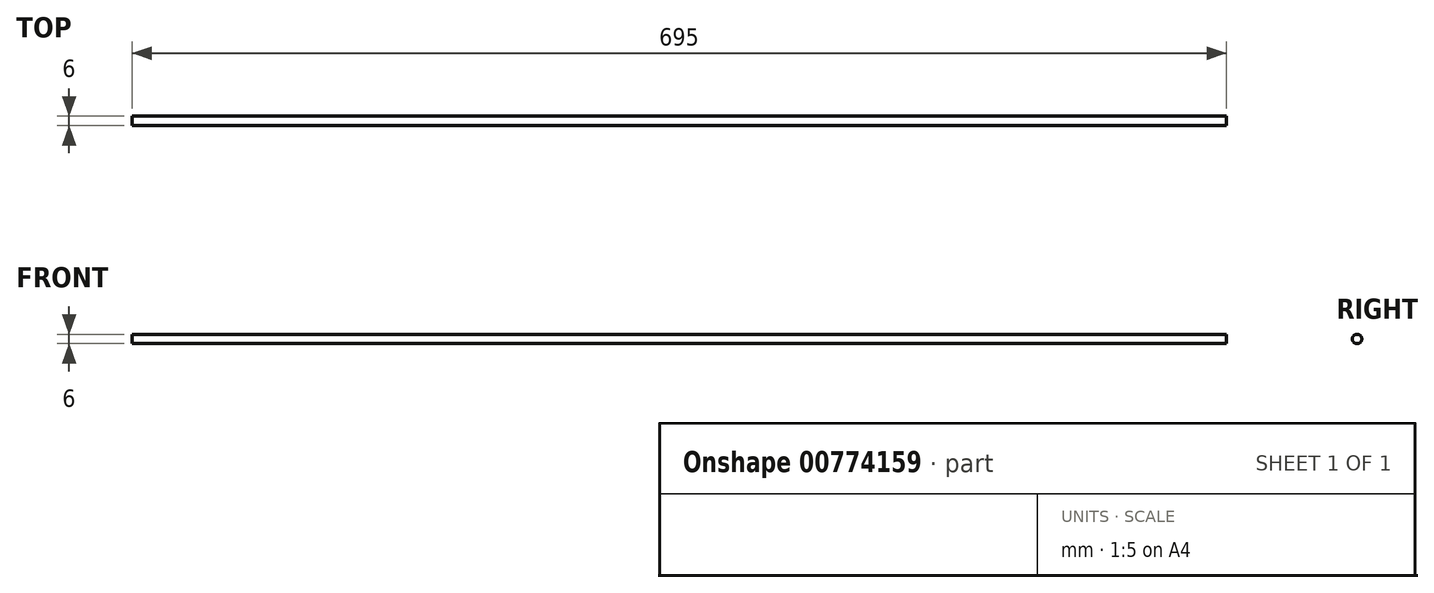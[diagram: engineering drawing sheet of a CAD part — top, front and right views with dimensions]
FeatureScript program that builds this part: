
annotation { "Feature Type Name" : "Feature", "Feature Type Description" : "" }
export const myFeature = defineFeature(function(context is Context, id is Id, definition is map)
    precondition{}
    {
        {
            var Q0;
            Q0=qCreatedBy(makeId("Front.planeOp"),FACE);
            var sketch = newSketch(context, id + "F0", { "sketchPlane" : qUnion([Q0])});
            skLineSegment(sketch, "E0.bottom", {"start": v(0, 0) * mm, "end": v(-695, 0) * mm});
            skLineSegment(sketch, "E0.top", {"start": v(0, -3) * mm, "end": v(-695, -3) * mm});
            skLineSegment(sketch, "E0.left", {"start": v(0, 0) * mm, "end": v(0, -3) * mm});
            skLineSegment(sketch, "E0.right", {"start": v(-695, 0) * mm, "end": v(-695, -3) * mm});
            skSolve(sketch);
        }
        {
            var Q0;
            Q0=makeQuery(id+"F0.imprint","IMPRINT",FACE,{"disambiguationData":[TD([[makeQuery(id+"F0.imprint","IMPRINT",EDGE,{"derivedFrom":sQuery(id+"F0.wireOp",EDGE,"E0.bottom")}),1.0]])]});
            var Q1;
            Q1=sQuery(id+"F0.wireOp",EDGE,"E0.bottom");
            revolve(context, id + "F1", {"surfaceOperationType" : NewSurfaceOperationType.NEW, "entities" : qUnion([Q0]), "axis" : qUnion([Q1]), "revolveType" : RevolveType.FULL});
        }
    });
